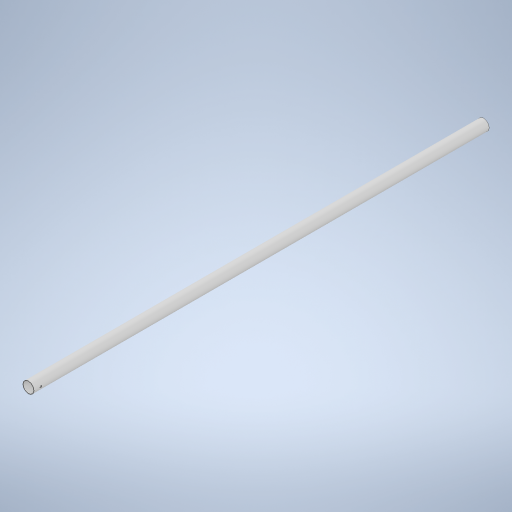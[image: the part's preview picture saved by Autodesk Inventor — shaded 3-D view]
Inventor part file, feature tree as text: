
AUTODESK INVENTOR PART (.ipt)
format: ipt  version: 2024 (Build 280153000, 153)  size: 250,880 bytes
history: native  units: mm
features: extrude x3, sketch x3
ambient origin geometry x8: Origin, YZ Plane, XZ Plane, XY Plane, X Axis, Y Axis, Z Axis, Center Point
bodies: Solid1 (feature_tree)
feature tree (6):
  extrude  "Extrusion1"  Depth=2000.0mm TaperAngle=0.0deg
  extrude  "Extrusion2"  Depth=2000.0mm TaperAngle=0.0deg
  extrude  "Extrusion3"  Depth=25.0mm
  sketch  "Sketch1"  dims[d0=50.0mm d1=2000.0mm d2=0.0mm]
  sketch  "Sketch2"  dims[d3=46.0mm d4=2000.0mm d5=0.0mm]
  sketch  "Sketch3"  dims[d6=9.0mm d7=30.0mm d8=25.0mm d9=0.0mm]
